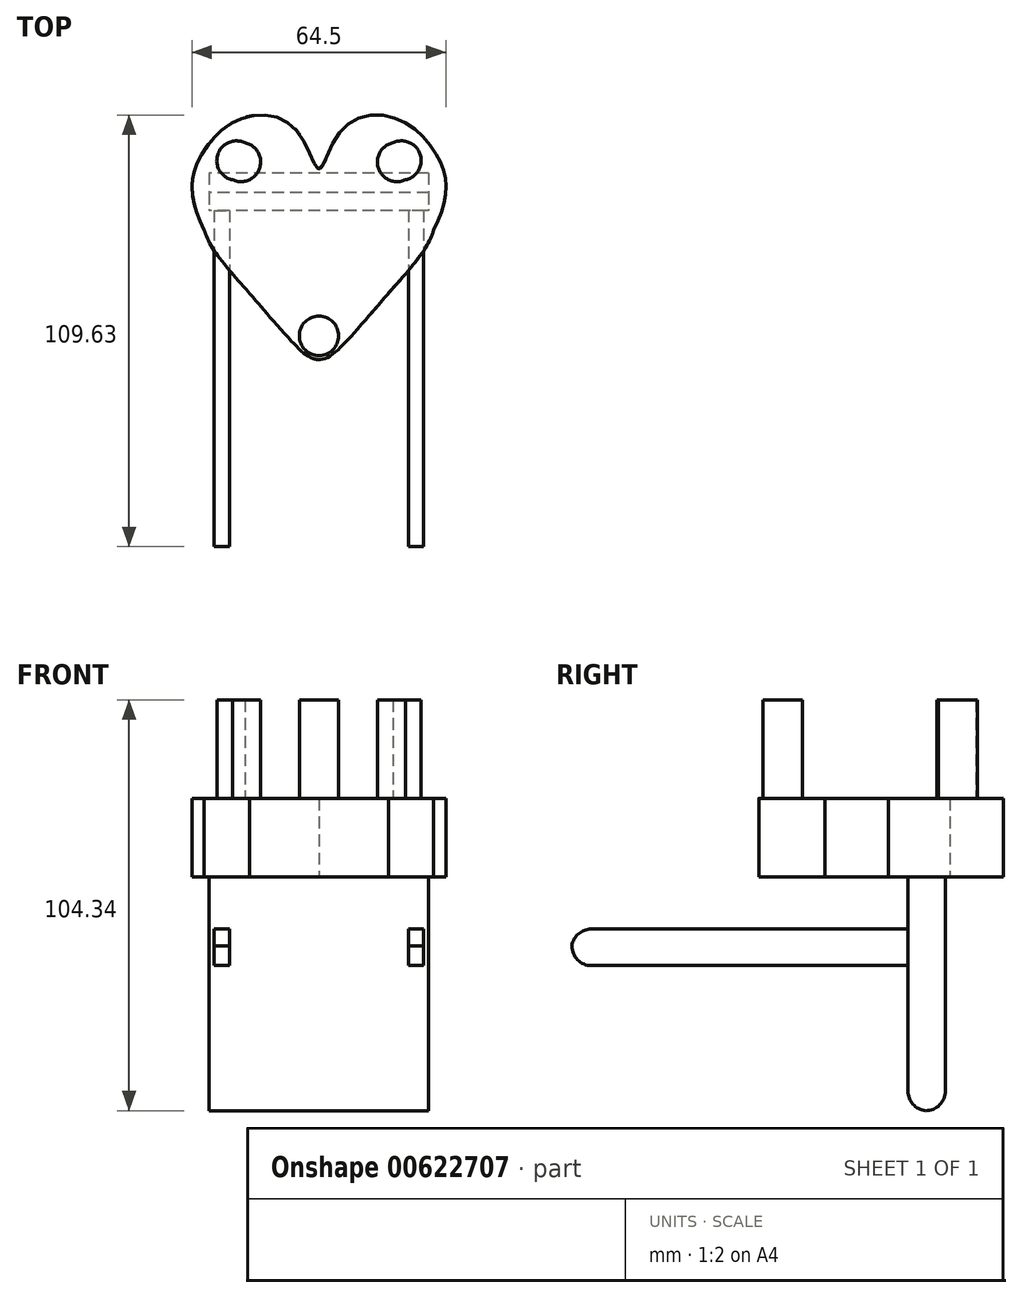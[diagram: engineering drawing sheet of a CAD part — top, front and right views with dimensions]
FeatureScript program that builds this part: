
annotation { "Feature Type Name" : "Feature", "Feature Type Description" : "" }
export const myFeature = defineFeature(function(context is Context, id is Id, definition is map)
    precondition{}
    {
        {
            var Q0;
            Q0=qCreatedBy(makeId("Top.planeOp"),FACE);
            var sketch = newSketch(context, id + "F0", { "sketchPlane" : qUnion([Q0])});
            skFitSpline(sketch, "E0", {"points": [v(0, 10.6) * mm, v(5.82, 20.53) * mm, v(19.57, 23.4) * mm, v(29.31, 14.99) * mm, v(32.18, 7.54) * mm, v(31.22, 0) * mm, v(25.5, -10.98) * mm, v(9.64, -30.27) * mm, v(0, -37.9) * mm, v(-9.26, -30.27) * mm, v(-26.45, -10.4) * mm, v(-29.88, -2.58) * mm, v(-31.8, 6.02) * mm, v(-30.65, 11.36) * mm, v(-23.2, 20.72) * mm, v(-6.4, 19.95) * mm, v(0, 10.6) * mm]});
            skSolve(sketch);
        }
        {
            var Q0;
            Q0 = qSketchRegion(id + "F0", true);
            extrude(context, id + "F1", {"entities" : qUnion([Q0]), "depth" : 20 * mm, "offsetDistance" : 25.4 * mm});
        }
        {
            var Q0;
            Q0=makeQuery(id+"F1.opExtrude","CAP_FACE",FACE,{"disambiguationData":[OSD([sQuery(id+"F0.wireOp",EDGE,"E0")])],"isStart":false});
            var sketch = newSketch(context, id + "F2", { "sketchPlane" : qUnion([Q0])});
            skCircle(sketch, "E1", {"center": v(20.96, 12.69) * mm, "radius": 5 * mm});
            skCircle(sketch, "E2", {"center": v(-19.83, 12.31) * mm, "radius": 5 * mm});
            skCircle(sketch, "E3", {"center": v(0, -31.86) * mm, "radius": 5 * mm});
            skSolve(sketch);
        }
        {
            var Q0;
            Q0=makeQuery(id+"F2.imprint","IMPRINT",FACE,{"disambiguationData":[TD([[makeQuery(id+"F2.imprint","IMPRINT",EDGE,{"derivedFrom":sQuery(id+"F2.wireOp",EDGE,"E2")}),1.0]])]});
            var Q1;
            Q1=makeQuery(id+"F2.imprint","IMPRINT",FACE,{"disambiguationData":[TD([[makeQuery(id+"F2.imprint","IMPRINT",EDGE,{"derivedFrom":sQuery(id+"F2.wireOp",EDGE,"E3")}),1.0]])]});
            var Q2;
            Q2=makeQuery(id+"F2.imprint","IMPRINT",FACE,{"disambiguationData":[TD([[makeQuery(id+"F2.imprint","IMPRINT",EDGE,{"derivedFrom":sQuery(id+"F2.wireOp",EDGE,"E1")}),1.0]])]});
            extrude(context, id + "F3", {"entities" : qUnion([Q0, Q1, Q2]), "operationType" : NewBodyOperationType.ADD, "depth" : 25 * mm, "offsetDistance" : 25 * mm});
        }
        {
            var Q0;
            Q0=qCreatedBy(makeId("Front.planeOp"),FACE);
            var sketch = newSketch(context, id + "F4", { "sketchPlane" : qUnion([Q0])});
            skLineSegment(sketch, "E4.bottom", {"start": v(27.88, 0) * mm, "end": v(-26.35, 0) * mm});
            skLineSegment(sketch, "E4.top", {"start": v(27.88, -59.34) * mm, "end": v(-26.35, -59.34) * mm});
            skLineSegment(sketch, "E4.left", {"start": v(27.88, 0) * mm, "end": v(27.88, -59.34) * mm});
            skLineSegment(sketch, "E4.right", {"start": v(-26.35, 0) * mm, "end": v(-26.35, -59.34) * mm});
            skSolve(sketch);
        }
        {
            var Q0;
            Q0 = qSketchRegion(id + "F4", true);
            extrude(context, id + "F5", {"entities" : qUnion([Q0]), "operationType" : NewBodyOperationType.ADD, "oppositeDirection" : true, "depth" : 9.5 * mm, "offsetDistance" : 25 * mm});
        }
        {
            var Q0;
            Q0=makeQuery(id+"F5.opExtrude","CAP_EDGE",EDGE,{"disambiguationData":[OSD([sQuery(id+"F4.wireOp",EDGE,"E4.top")])],"isStart":false});
            fillet(context, id + "F6", {"entities" : qUnion([Q0]), "radius" : 5 * mm, "tangentPropagation" : true, "allowEdgeOverflow" : false});
        }
        {
            var Q0;
            Q0=makeQuery(id+"F5.opExtrude","CAP_EDGE",EDGE,{"disambiguationData":[OSD([sQuery(id+"F4.wireOp",EDGE,"E4.top")])],"isStart":true});
            fillet(context, id + "F7", {"entities" : qUnion([Q0]), "radius" : 5 * mm, "tangentPropagation" : true, "allowEdgeOverflow" : false});
        }
        {
            var Q0;
            Q0=qCreatedBy(makeId("Right.planeOp"),FACE);
            cPlane(context, id + "F8", {"entities" : qUnion([Q0]), "cplaneType" : CPlaneType.OFFSET, "offset" : 22.7 * mm, "width" : 150 * mm, "height" : 150 * mm});
        }
        {
            var Q0;
            Q0=qCreatedBy(id+"F8.planeOp",FACE);
            var sketch = newSketch(context, id + "F9", { "sketchPlane" : qUnion([Q0])});
            skLineSegment(sketch, "E5.bottom", {"start": v(0, -22.48) * mm, "end": v(-85.38, -22.48) * mm});
            skLineSegment(sketch, "E5.top", {"start": v(0, -13.17) * mm, "end": v(-85.38, -13.17) * mm});
            skLineSegment(sketch, "E5.left", {"start": v(0, -22.48) * mm, "end": v(0, -13.17) * mm});
            skLineSegment(sketch, "E5.right", {"start": v(-85.38, -22.48) * mm, "end": v(-85.38, -13.17) * mm});
            skSolve(sketch);
        }
        {
            var Q0;
            Q0 = qSketchRegion(id + "F9", true);
            extrude(context, id + "F10", {"entities" : qUnion([Q0]), "operationType" : NewBodyOperationType.ADD, "depth" : 3.9 * mm, "offsetDistance" : 25 * mm});
        }
        {
            var Q0;
            Q0=makeQuery(id+"F1.opExtrude","SWEPT_BODY",BODY,{"disambiguationData":[OSD([sQuery(id+"F0.wireOp",EDGE,"E0")])]});
            var Q1;
            Q1=qCreatedBy(makeId("Right.planeOp"),FACE);
            mirror(context, id + "F11", {"operationType" : NewBodyOperationType.ADD, "entities" : qUnion([Q0]), "mirrorPlane" : qUnion([Q1])});
        }
        {
            var Q0;
            Q0=makeQuery(id+"F11.opPattern","COPY",EDGE,{"derivedFrom":makeQuery(id+"F10.opExtrude","SWEPT_EDGE",EDGE,{"disambiguationData":[OSD([sQuery(id+"F9.wireOp",EDGE,"E5.bottom"),sQuery(id+"F9.wireOp",EDGE,"E5.right")])]}),"instanceName":"1"});
            fillet(context, id + "F12", {"entities" : qUnion([Q0]), "radius" : 5 * mm, "tangentPropagation" : true, "allowEdgeOverflow" : false});
        }
        {
            var Q0;
            Q0=makeQuery(id+"F10.opExtrude","SWEPT_EDGE",EDGE,{"disambiguationData":[OSD([sQuery(id+"F9.wireOp",EDGE,"E5.bottom"),sQuery(id+"F9.wireOp",EDGE,"E5.right")])]});
            fillet(context, id + "F13", {"entities" : qUnion([Q0]), "radius" : 5 * mm, "tangentPropagation" : true, "allowEdgeOverflow" : false});
        }
        {
            var Q0;
            Q0=makeQuery(id+"F10.opExtrude","SWEPT_EDGE",EDGE,{"disambiguationData":[OSD([sQuery(id+"F9.wireOp",EDGE,"E5.top"),sQuery(id+"F9.wireOp",EDGE,"E5.right")])]});
            fillet(context, id + "F14", {"entities" : qUnion([Q0]), "radius" : 5 * mm, "tangentPropagation" : true, "allowEdgeOverflow" : false});
        }
        {
            var Q0;
            Q0=makeQuery(id+"F11.opPattern","COPY",EDGE,{"derivedFrom":makeQuery(id+"F10.opExtrude","SWEPT_EDGE",EDGE,{"disambiguationData":[OSD([sQuery(id+"F9.wireOp",EDGE,"E5.top"),sQuery(id+"F9.wireOp",EDGE,"E5.right")])]}),"instanceName":"1"});
            fillet(context, id + "F15", {"entities" : qUnion([Q0]), "radius" : 5 * mm, "tangentPropagation" : true, "allowEdgeOverflow" : false});
        }
    });
